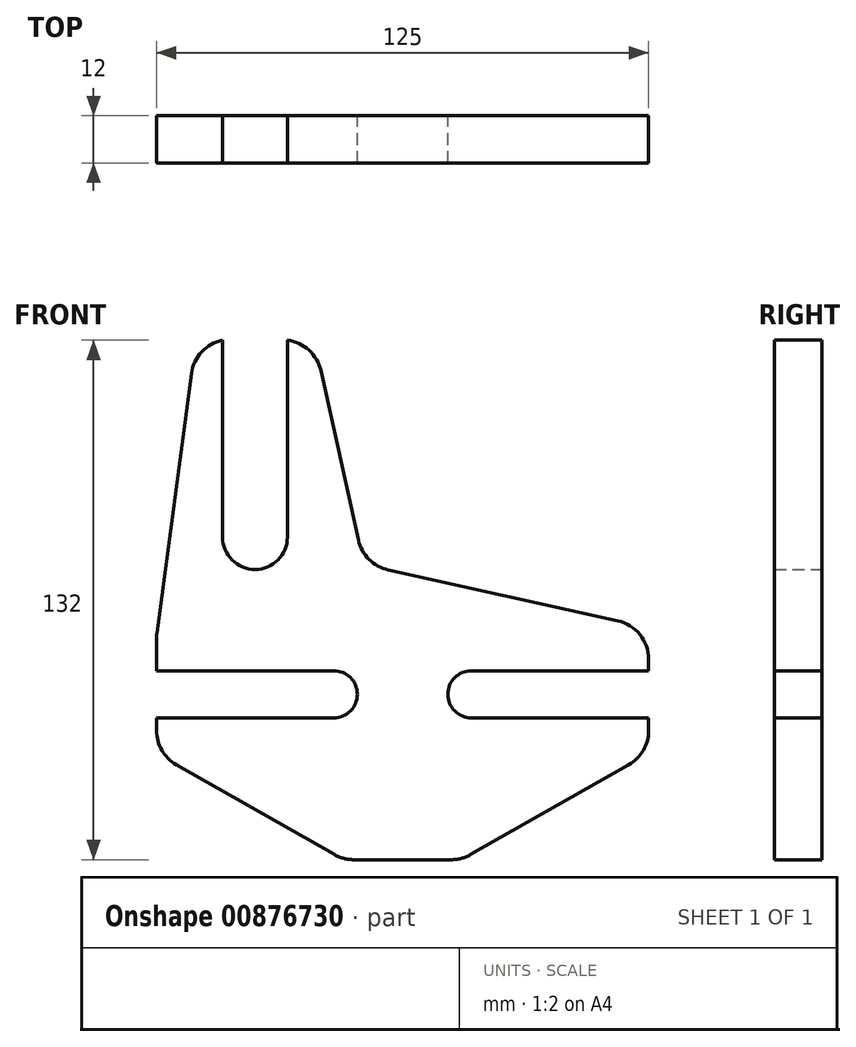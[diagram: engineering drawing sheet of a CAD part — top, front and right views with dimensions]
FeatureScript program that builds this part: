
annotation { "Feature Type Name" : "Feature", "Feature Type Description" : "" }
export const myFeature = defineFeature(function(context is Context, id is Id, definition is map)
    precondition{}
    {
        {
            var Q0;
            Q0=qCreatedBy(makeId("Front.planeOp"),FACE);
            var sketch = newSketch(context, id + "F0", { "sketchPlane" : qUnion([Q0])});
            skCircle(sketch, "E0", {"center": v(-37.5, 0) * mm, "radius": 6 * mm, "construction": true});
            skCircle(sketch, "E1", {"center": v(37.5, 0) * mm, "radius": 6 * mm, "construction": true});
            skLineSegment(sketch, "E2", {"start": v(-62.5, 15) * mm, "end": v(-52.5, 90) * mm});
            skLineSegment(sketch, "E3", {"start": v(-52.5, 90) * mm, "end": v(-45.75, 90) * mm});
            skLineSegment(sketch, "E4", {"start": v(-22.5, 90) * mm, "end": v(-9.86, 33) * mm});
            skLineSegment(sketch, "E5", {"start": v(-9.86, 33) * mm, "end": v(62.5, 16.96) * mm});
            skLineSegment(sketch, "E6", {"start": v(62.5, 16.96) * mm, "end": v(62.5, 6) * mm});
            skLineSegment(sketch, "E7", {"start": v(62.5, -15) * mm, "end": v(15, -42) * mm});
            skLineSegment(sketch, "E8", {"start": v(15, -42) * mm, "end": v(-15, -42) * mm});
            skLineSegment(sketch, "E9", {"start": v(-15, -42) * mm, "end": v(-62.5, -15) * mm});
            skLineSegment(sketch, "E10", {"start": v(-62.5, -15) * mm, "end": v(-62.5, -6) * mm});
            skLineSegment(sketch, "E11", {"start": v(-37.5, 0) * mm, "end": v(-37.5, 90) * mm, "construction": true});
            skLineSegment(sketch, "E12", {"start": v(0, -42) * mm, "end": v(0, 98.83) * mm, "construction": true});
            skLineSegment(sketch, "E13", {"start": v(-62.5, 0) * mm, "end": v(62.5, 0) * mm, "construction": true});
            skLineSegment(sketch, "E14", {"start": v(-62.5, 6) * mm, "end": v(-17.5, 6) * mm});
            skLineSegment(sketch, "E15", {"start": v(-62.5, -6) * mm, "end": v(-17.5, -6) * mm});
            skArc(sketch, "E16", {"start": v(-17.5, -6) * mm, "mid": v(-11.5, 0) * mm, "end": v(-17.5, 6) * mm});
            skArc(sketch, "E17", {"start": v(17.5, 6) * mm, "mid": v(11.5, 0) * mm, "end": v(17.5, -6) * mm});
            skLineSegment(sketch, "E18.trimOffspring", {"start": v(17.5, 6) * mm, "end": v(62.5, 6) * mm});
            skLineSegment(sketch, "E19.trimOffspring", {"start": v(17.5, -6) * mm, "end": v(62.5, -6) * mm});
            skArc(sketch, "E20", {"start": v(-45.75, 40) * mm, "mid": v(-37.5, 31.75) * mm, "end": v(-29.25, 40) * mm});
            skLineSegment(sketch, "E21", {"start": v(-29.25, 40) * mm, "end": v(-29.25, 90) * mm});
            skLineSegment(sketch, "E22", {"start": v(-45.75, 40) * mm, "end": v(-45.75, 90) * mm});
            skLineSegment(sketch, "E23.trimOffspring", {"start": v(-62.5, 6) * mm, "end": v(-62.5, 15) * mm});
            skLineSegment(sketch, "E24.trimOffspring", {"start": v(62.5, -6) * mm, "end": v(62.5, -15) * mm});
            skLineSegment(sketch, "E25.trimOffspring", {"start": v(-29.25, 90) * mm, "end": v(-22.5, 90) * mm});
            skSolve(sketch);
        }
        {
            var Q0;
            Q0 = qSketchRegion(id + "F0", true);
            extrude(context, id + "F1", {"entities" : qUnion([Q0]), "depth" : 12 * mm, "offsetDistance" : 25 * mm});
        }
        {
            var Q0;
            Q0=makeQuery(id+"F1.opExtrude","SWEPT_EDGE",EDGE,{"disambiguationData":[OSD([sQuery(id+"F0.wireOp",EDGE,"E2"),sQuery(id+"F0.wireOp",EDGE,"E3")])]});
            var Q1;
            Q1=makeQuery(id+"F1.opExtrude","SWEPT_EDGE",EDGE,{"disambiguationData":[OSD([sQuery(id+"F0.wireOp",EDGE,"E2"),sQuery(id+"F0.wireOp",EDGE,"E23.trimOffspring")])]});
            var Q2;
            Q2=makeQuery(id+"F1.opExtrude","SWEPT_EDGE",EDGE,{"disambiguationData":[OSD([sQuery(id+"F0.wireOp",EDGE,"E9"),sQuery(id+"F0.wireOp",EDGE,"E10")])]});
            var Q3;
            Q3=makeQuery(id+"F1.opExtrude","SWEPT_EDGE",EDGE,{"disambiguationData":[OSD([sQuery(id+"F0.wireOp",EDGE,"E8"),sQuery(id+"F0.wireOp",EDGE,"E9")])]});
            var Q4;
            Q4=makeQuery(id+"F1.opExtrude","SWEPT_EDGE",EDGE,{"disambiguationData":[OSD([sQuery(id+"F0.wireOp",EDGE,"E7"),sQuery(id+"F0.wireOp",EDGE,"E8")])]});
            var Q5;
            Q5=makeQuery(id+"F1.opExtrude","SWEPT_EDGE",EDGE,{"disambiguationData":[OSD([sQuery(id+"F0.wireOp",EDGE,"E7"),sQuery(id+"F0.wireOp",EDGE,"E24.trimOffspring")])]});
            var Q6;
            Q6=makeQuery(id+"F1.opExtrude","SWEPT_EDGE",EDGE,{"disambiguationData":[OSD([sQuery(id+"F0.wireOp",EDGE,"E5"),sQuery(id+"F0.wireOp",EDGE,"E6")])]});
            var Q7;
            Q7=makeQuery(id+"F1.opExtrude","SWEPT_EDGE",EDGE,{"disambiguationData":[OSD([sQuery(id+"F0.wireOp",EDGE,"E4"),sQuery(id+"F0.wireOp",EDGE,"E5")])]});
            var Q8;
            Q8=makeQuery(id+"F1.opExtrude","SWEPT_EDGE",EDGE,{"disambiguationData":[OSD([sQuery(id+"F0.wireOp",EDGE,"E4"),sQuery(id+"F0.wireOp",EDGE,"E25.trimOffspring")])]});
            fillet(context, id + "F2", {"entities" : qUnion([Q0, Q1, Q2, Q3, Q4, Q5, Q6, Q7, Q8]), "radius" : 10 * mm, "tangentPropagation" : true, "allowEdgeOverflow" : false});
        }
    });
